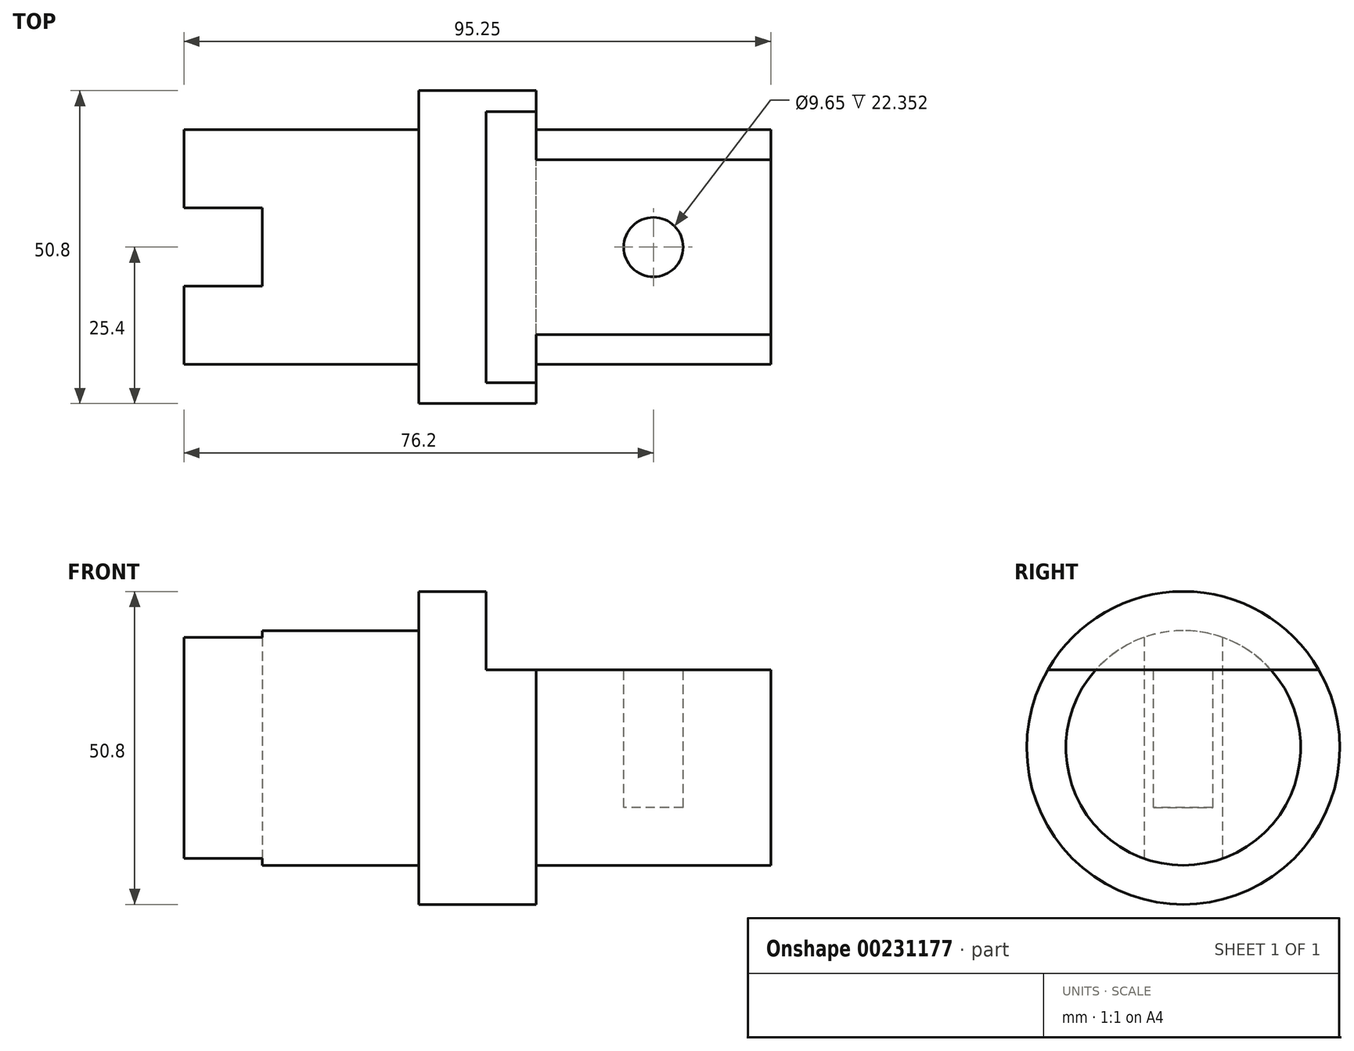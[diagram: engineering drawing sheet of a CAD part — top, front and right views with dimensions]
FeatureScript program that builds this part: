
annotation { "Feature Type Name" : "Feature", "Feature Type Description" : "" }
export const myFeature = defineFeature(function(context is Context, id is Id, definition is map)
    precondition{}
    {
        {
            var Q0;
            Q0=qCreatedBy(makeId("Right.planeOp"),FACE);
            var sketch = newSketch(context, id + "F0", { "sketchPlane" : qUnion([Q0])});
            skCircle(sketch, "E0", {"center": v(0, 0) * mm, "radius": 25.4 * mm});
            skSolve(sketch);
        }
        {
            var Q0;
            Q0=makeQuery(id+"F0.imprint","IMPRINT",FACE,{"disambiguationData":[TD([[makeQuery(id+"F0.imprint","IMPRINT",EDGE,{"derivedFrom":sQuery(id+"F0.wireOp",EDGE,"E0")}),1.0]])]});
            extrude(context, id + "F1", {"entities" : qUnion([Q0]), "depth" : 95.25 * mm});
        }
        {
            var Q0;
            Q0=makeQuery(id+"F1.opExtrude","CAP_FACE",FACE,{"disambiguationData":[OSD([sQuery(id+"F0.wireOp",EDGE,"E0")])],"isStart":false});
            var sketch = newSketch(context, id + "F2", { "sketchPlane" : qUnion([Q0])});
            skCircle(sketch, "E1", {"center": v(0, 0) * mm, "radius": 19.05 * mm});
            skSolve(sketch);
        }
        {
            var Q0;
            Q0=makeQuery(id+"F2.imprint","IMPRINT",FACE,{"disambiguationData":[TD([[makeQuery(id+"F2.imprint","IMPRINT",EDGE,{"derivedFrom":sQuery(id+"F2.wireOp",EDGE,"E1")}),-1.0]])]});
            extrude(context, id + "F3", {"entities" : qUnion([Q0]), "operationType" : NewBodyOperationType.REMOVE, "oppositeDirection" : true, "depth" : 38.1 * mm});
        }
        {
            var Q0;
            Q0=makeQuery(id+"F1.opExtrude","CAP_FACE",FACE,{"disambiguationData":[OSD([sQuery(id+"F0.wireOp",EDGE,"E0")])],"isStart":true});
            var sketch = newSketch(context, id + "F4", { "sketchPlane" : qUnion([Q0])});
            skCircle(sketch, "E2", {"center": v(0, 0) * mm, "radius": 19.05 * mm});
            skSolve(sketch);
        }
        {
            var Q0;
            Q0=makeQuery(id+"F4.imprint","IMPRINT",FACE,{"disambiguationData":[TD([[makeQuery(id+"F4.imprint","IMPRINT",EDGE,{"derivedFrom":sQuery(id+"F4.wireOp",EDGE,"E2")}),-1.0]])]});
            extrude(context, id + "F5", {"entities" : qUnion([Q0]), "operationType" : NewBodyOperationType.REMOVE, "oppositeDirection" : true, "depth" : 38.1 * mm});
        }
        {
            var Q0;
            Q0=makeQuery(id+"F1.opExtrude","CAP_FACE",FACE,{"disambiguationData":[OSD([sQuery(id+"F0.wireOp",EDGE,"E0")])],"isStart":true});
            var sketch = newSketch(context, id + "F6", { "sketchPlane" : qUnion([Q0])});
            skLineSegment(sketch, "E3.bottom", {"start": v(6.35, 19.05) * mm, "end": v(-6.35, 19.05) * mm});
            skLineSegment(sketch, "E3.top", {"start": v(6.35, -19.05) * mm, "end": v(-6.35, -19.05) * mm});
            skLineSegment(sketch, "E3.left", {"start": v(6.35, 19.05) * mm, "end": v(6.35, -19.05) * mm});
            skLineSegment(sketch, "E3.right", {"start": v(-6.35, 19.05) * mm, "end": v(-6.35, -19.05) * mm});
            skPoint(sketch, "E3.middle", {"position": v(0, 0) * mm});
            skSolve(sketch);
        }
        {
            var Q0;
            {var subQ0=makeQuery(id+"F5.boolean.opBoolean","COPY",EDGE,{"derivedFrom":makeQuery(id+"F5.opExtrude","CAP_EDGE",EDGE,{"disambiguationData":[OSD([sQuery(id+"F4.wireOp",EDGE,"E2")])],"isStart":true})});var subQ5=sQuery(id+"F6.wireOp",EDGE,"E3.left");var subQ6=makeQuery(id+"F6.imprint","INTERSECT",VERTEX,{"disambiguationData":[OD(0.0)],"derivedFrom":[subQ0,subQ5]});Q0=makeQuery(id+"F6.imprint","IMPRINT",FACE,{"disambiguationData":[TD([[makeQuery(id+"F6.imprint","IMPRINT",EDGE,{"disambiguationData":[TD([[subQ6,-1.0]])],"derivedFrom":subQ5}),-1.0]])]});}
            extrude(context, id + "F7", {"entities" : qUnion([Q0]), "operationType" : NewBodyOperationType.REMOVE, "oppositeDirection" : true, "depth" : 12.7 * mm});
        }
        {
            var Q0;
            Q0=makeQuery(id+"F1.opExtrude","CAP_FACE",FACE,{"disambiguationData":[OSD([sQuery(id+"F0.wireOp",EDGE,"E0")])],"isStart":false});
            var sketch = newSketch(context, id + "F8", { "sketchPlane" : qUnion([Q0])});
            skLineSegment(sketch, "E4.left", {"start": v(-40.06, 21.54) * mm, "end": v(-40.06, 12.7) * mm});
            skPoint(sketch, "E4.middle", {"position": v(-36.2, 9.5) * mm});
            skLineSegment(sketch, "E5.bottom", {"start": v(36.14, 12.7) * mm, "end": v(-40.06, 12.7) * mm});
            skLineSegment(sketch, "E5.top", {"start": v(36.14, 25.4) * mm, "end": v(-40.06, 25.4) * mm});
            skLineSegment(sketch, "E5.left", {"start": v(36.14, 12.7) * mm, "end": v(36.14, 25.4) * mm});
            skLineSegment(sketch, "E5.right", {"start": v(-40.06, 21.54) * mm, "end": v(-40.06, 25.4) * mm});
            skPoint(sketch, "E4.bottom.end.orphan", {"position": v(-32.36, 21.54) * mm});
            skPoint(sketch, "E4.top.end.orphan", {"position": v(-32.36, -2.53) * mm});
            skPoint(sketch, "E4.top.start.orphan", {"position": v(-40.06, -2.53) * mm});
            skSolve(sketch);
        }
        {
            var Q0;
            {var subQ1=sQuery(id+"F8.wireOp",EDGE,"E4.left");Q0=makeQuery(id+"F8.imprint","IMPRINT",FACE,{"disambiguationData":[TD([[makeQuery(id+"F8.imprint","IMPRINT",EDGE,{"derivedFrom":subQ1}),1.0]])]});}
            var Q1;
            {var subQ0=sQuery(id+"F8.wireOp",EDGE,"E5.bottom");var subQ1=makeQuery(id+"F3.boolean.opBoolean","COPY",EDGE,{"derivedFrom":makeQuery(id+"F3.opExtrude","CAP_EDGE",EDGE,{"disambiguationData":[OSD([sQuery(id+"F2.wireOp",EDGE,"E1")])],"isStart":true})});var subQ2=makeQuery(id+"F8.imprint","INTERSECT",VERTEX,{"disambiguationData":[OD(0.0)],"derivedFrom":[subQ1,subQ0]});Q1=makeQuery(id+"F8.imprint","IMPRINT",FACE,{"disambiguationData":[TD([[makeQuery(id+"F8.imprint","IMPRINT",EDGE,{"disambiguationData":[TD([[subQ2,-1.0]])],"derivedFrom":subQ0}),-1.0]])]});}
            extrude(context, id + "F9", {"entities" : qUnion([Q0, Q1]), "operationType" : NewBodyOperationType.REMOVE, "oppositeDirection" : true, "depth" : 46.23 * mm});
        }
        {
            var Q0;
            Q0=makeQuery(id+"F9.boolean.opBoolean","COPY",FACE,{"derivedFrom":makeQuery(id+"F9.opExtrude","SWEPT_FACE",FACE,{"disambiguationData":[OSD([sQuery(id+"F8.wireOp",EDGE,"E5.bottom")])]})});
            var sketch = newSketch(context, id + "F10", { "sketchPlane" : qUnion([Q0])});
            skCircle(sketch, "E6", {"center": v(76.2, 0) * mm, "radius": 4.83 * mm});
            skSolve(sketch);
        }
        {
            var Q0;
            Q0=makeQuery(id+"F10.imprint","IMPRINT",FACE,{"disambiguationData":[TD([[makeQuery(id+"F10.imprint","IMPRINT",EDGE,{"derivedFrom":sQuery(id+"F10.wireOp",EDGE,"E6")}),1.0]])]});
            extrude(context, id + "F11", {"entities" : qUnion([Q0]), "operationType" : NewBodyOperationType.REMOVE, "oppositeDirection" : true, "depth" : 22.35 * mm});
        }
    });
